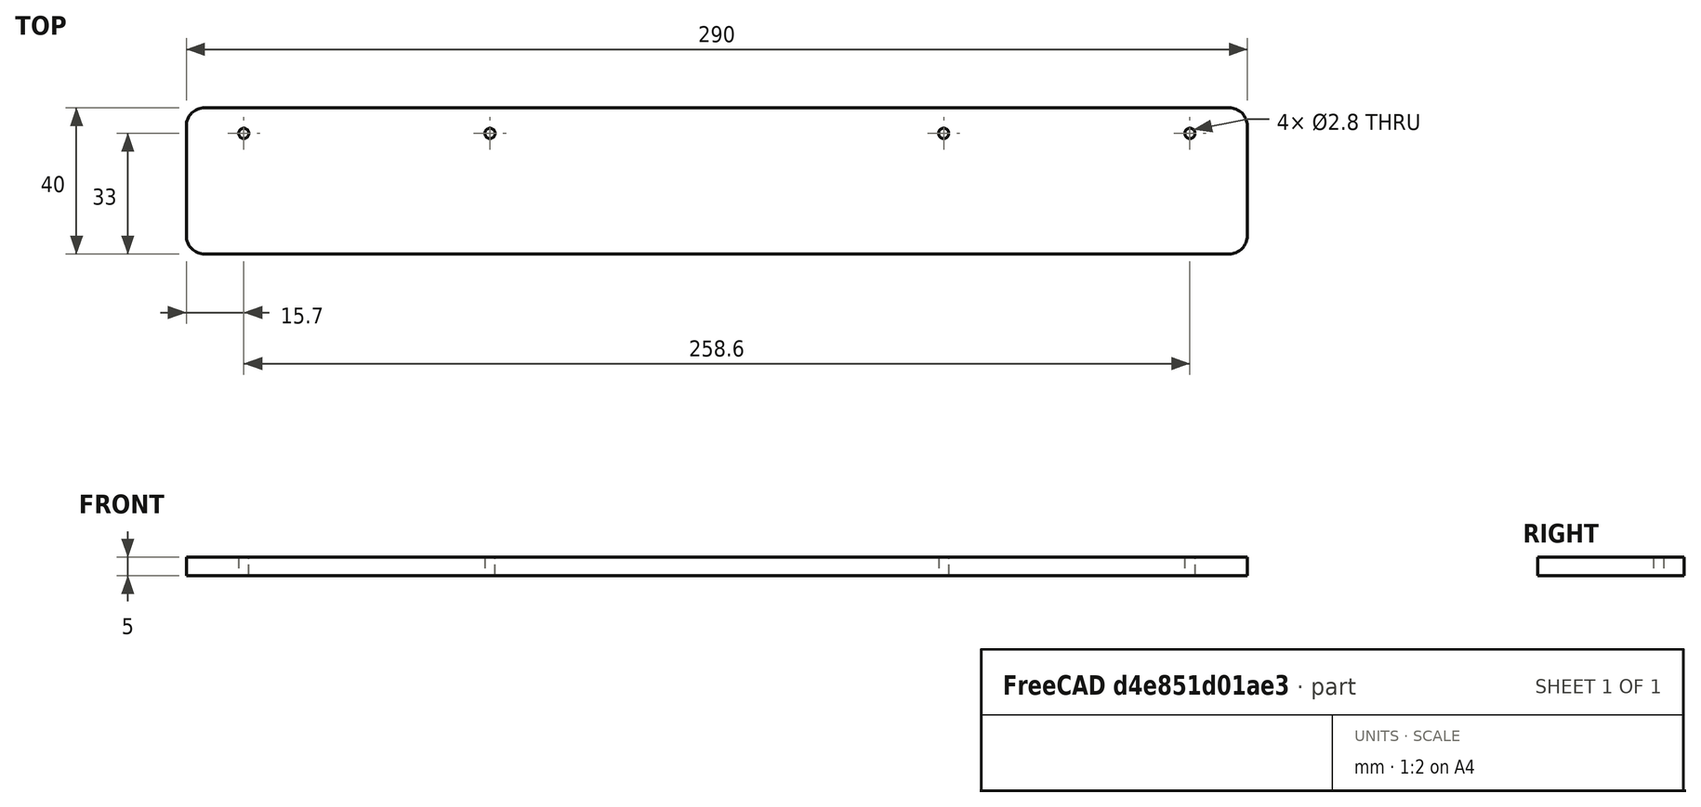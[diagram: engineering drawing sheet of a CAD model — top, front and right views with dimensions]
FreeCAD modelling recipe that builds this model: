
FCSTD DOCUMENT  (FreeCAD 1.0R39109 (Git))
Label: CasePodsHolder
License: Creative Commons Attribution 4.0
LicenseURL: https://creativecommons.org/licenses/by/4.0/
objects: Sketcher::SketchObject×1, PartDesign::Pad×1, PartDesign::Body×1
note: 6 computed .brp shape members not serialized (recipe doc carries the construction recipe); baked Part::Feature solids carry a one-line shape summary decoded from their .brp

FEATURE [Sketcher::SketchObject] Sketch
  ArcFitTolerance = 1e-06
  AttachmentSupport = -> [XY_Plane]
  FullyConstrained = true
  MakeInternals = false
  MapMode = 5
  sketch-geometry (14):
    g0: LineSegment StartX=-145 StartY=15 StartZ=0 EndX=-145 EndY=-15 EndZ=0
    g1: LineSegment StartX=-140 StartY=-20 StartZ=0 EndX=140 EndY=-20 EndZ=0
    g2: LineSegment StartX=145 StartY=-15 StartZ=0 EndX=145 EndY=15 EndZ=0
    g3: LineSegment StartX=140 StartY=20 StartZ=0 EndX=-140 EndY=20 EndZ=0
    g4: ArcOfCircle CenterX=-140 CenterY=15 CenterZ=0 NormalX=0 NormalY=0 NormalZ=1 AngleXU=0 Radius=5 StartAngle=1.5708 EndAngle=3.14159
    g5: ArcOfCircle CenterX=-140 CenterY=-15 CenterZ=0 NormalX=0 NormalY=0 NormalZ=1 AngleXU=0 Radius=5 StartAngle=3.14159 EndAngle=4.71239
    g6: ArcOfCircle CenterX=140 CenterY=-15 CenterZ=0 NormalX=0 NormalY=0 NormalZ=1 AngleXU=0 Radius=5 StartAngle=4.71239 EndAngle=6.28319
    g7: ArcOfCircle CenterX=140 CenterY=15 CenterZ=0 NormalX=0 NormalY=0 NormalZ=1 AngleXU=0 Radius=5 StartAngle=1e-16 EndAngle=1.5708
    g8: GeomPoint [constr] X=-145 Y=20 Z=0
    g9: GeomPoint [constr] X=145 Y=-20 Z=0
    g10: Circle CenterX=-62 CenterY=13 CenterZ=0 NormalX=0 NormalY=0 NormalZ=1 AngleXU=0 Radius=1.4
    g11: Circle CenterX=62 CenterY=13 CenterZ=0 NormalX=0 NormalY=0 NormalZ=1 AngleXU=0 Radius=1.4
    g12: Circle CenterX=-129.3 CenterY=13 CenterZ=0 NormalX=0 NormalY=0 NormalZ=1 AngleXU=0 Radius=1.4
    g13: Circle CenterX=129.3 CenterY=13 CenterZ=0 NormalX=0 NormalY=0 NormalZ=1 AngleXU=0 Radius=1.4
  constraints (33):
    c: Tangent(g0,g4) = -1.5708
    c: Tangent(g0,g5) = -1.5708
    c: Tangent(g1,g5) = -1.5708
    c: Tangent(g1,g6) = -1.5708
    c: Tangent(g2,g6) = -1.5708
    c: Tangent(g2,g7) = -1.5708
    c: Tangent(g3,g7) = -1.5708
    c: Tangent(g3,g4) = -1.5708
    c: Vertical(g0)
    c: Vertical(g2)
    c: Horizontal(g1)
    c: Horizontal(g3)
    c: Equal(g4,g5)
    c: Equal(g5,g6)
    c: Equal(g6,g7)
    c: PointOnObject(g8,g0)
    c: PointOnObject(g8,g3)
    c: PointOnObject(g9,g1)
    c: PointOnObject(g9,g2)
    c: Distance(g0,g2) = 290
    c: Distance(g1,g3) = 40
    c: Radius(g5) = 5
    c: Symmetric(g8,g9,g-1)
    c: Diameter(g10) = 2.8
    c: Symmetric(g10,g11,g-2)
    c: Equal(g10,g11)
    c: DistanceX(g10,g11) = 124
    c: Symmetric(g12,g13,g-2)
    c: Horizontal(g12,g10)
    c: DistanceX(g12,g10) = 67.3
    c: Equal(g12,g10)
    c: Equal(g10,g13)
    c: DistanceY(g12,g8) = 7
FEATURE [PartDesign::Pad] Pad
  Direction = (0,0,1)
  Length = 5
  Length2 = 10
  Profile = -> Sketch
  ReferenceAxis = -> Sketch [N_Axis]
  Suppressed = false
  Type = 0
FEATURE [PartDesign::Body] Body
  AllowCompound = false
  Group = -> [Sketch,Pad]
  Origin = -> Origin
  Tip = -> Pad
